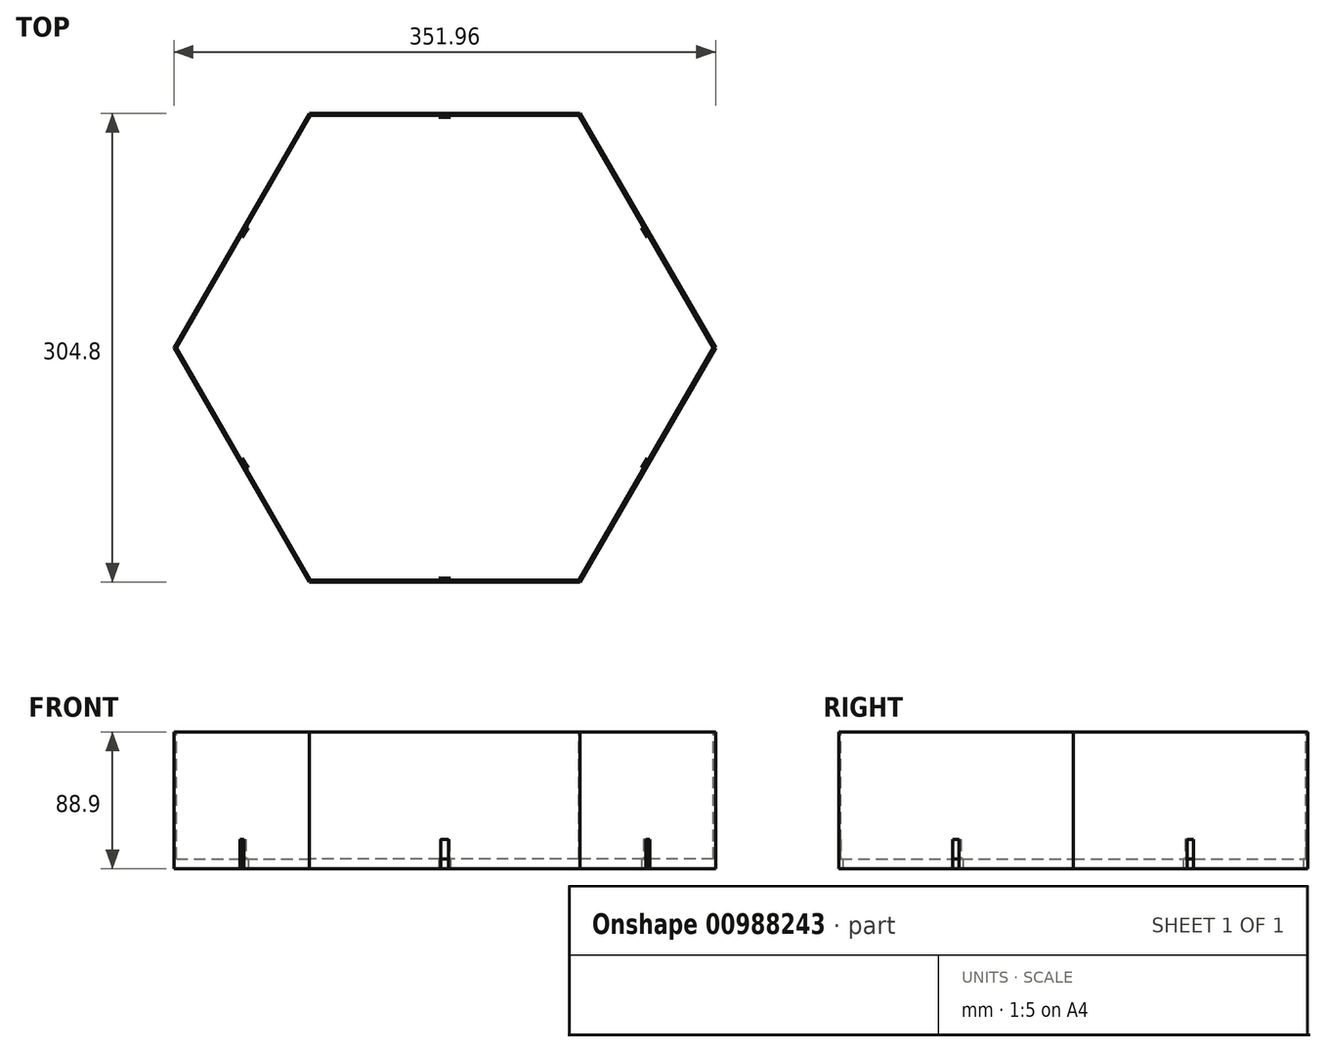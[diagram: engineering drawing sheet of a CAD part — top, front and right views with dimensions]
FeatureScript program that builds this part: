
annotation { "Feature Type Name" : "Feature", "Feature Type Description" : "" }
export const myFeature = defineFeature(function(context is Context, id is Id, definition is map)
    precondition{}
    {
        {
            var Q0;
            Q0=qCreatedBy(makeId("Top.planeOp"),FACE);
            var sketch = newSketch(context, id + "F0", { "sketchPlane" : qUnion([Q0])});
            skCircle(sketch, "E0.cCircle", {"center": v(0, 0) * mm, "radius": 152.4 * mm, "construction": true});
            skLineSegment(sketch, "E0.0", {"start": v(87.99, -152.4) * mm, "end": v(-87.99, -152.4) * mm});
            skLineSegment(sketch, "E0.1", {"start": v(-87.99, -152.4) * mm, "end": v(-175.98, 0) * mm});
            skLineSegment(sketch, "E0.2", {"start": v(-175.98, 0) * mm, "end": v(-87.99, 152.4) * mm});
            skLineSegment(sketch, "E0.3", {"start": v(-87.99, 152.4) * mm, "end": v(87.99, 152.4) * mm});
            skLineSegment(sketch, "E0.4", {"start": v(87.99, 152.4) * mm, "end": v(175.98, 0) * mm});
            skLineSegment(sketch, "E0.5", {"start": v(175.98, 0) * mm, "end": v(87.99, -152.4) * mm});
            skPoint(sketch, "E0.0.midPoint", {"position": v(0, -152.4) * mm});
            skSolve(sketch);
        }
        {
            var Q0;
            Q0=makeQuery(id+"F0.imprint","IMPRINT",FACE,{"disambiguationData":[TD([[makeQuery(id+"F0.imprint","IMPRINT",EDGE,{"derivedFrom":sQuery(id+"F0.wireOp",EDGE,"E0.0")}),-1.0]])]});
            extrude(context, id + "F1", {"entities" : qUnion([Q0]), "depth" : 88.9 * mm, "offsetDistance" : 25.4 * mm});
        }
        {
            var Q0;
            Q0=makeQuery(id+"F1.opExtrude","CAP_FACE",FACE,{"disambiguationData":[OSD([sQuery(id+"F0.wireOp",EDGE,"E0.0"),sQuery(id+"F0.wireOp",EDGE,"E0.1"),sQuery(id+"F0.wireOp",EDGE,"E0.2"),sQuery(id+"F0.wireOp",EDGE,"E0.3"),sQuery(id+"F0.wireOp",EDGE,"E0.4"),sQuery(id+"F0.wireOp",EDGE,"E0.5")])],"isStart":true});
            var sketch = newSketch(context, id + "F2", { "sketchPlane" : qUnion([Q0])});
            skLineSegment(sketch, "E1", {"start": v(0, 152.4) * mm, "end": v(0, -152.4) * mm});
            skLineSegment(sketch, "E2", {"start": v(-131.98, -76.2) * mm, "end": v(131.98, 76.2) * mm});
            skLineSegment(sketch, "E3", {"start": v(-131.98, 76.2) * mm, "end": v(131.98, -76.2) * mm});
            skLineSegment(sketch, "E4", {"start": v(87.99, 152.4) * mm, "end": v(-87.99, -152.4) * mm});
            skLineSegment(sketch, "E5", {"start": v(-87.99, 152.4) * mm, "end": v(87.99, -152.4) * mm});
            skLineSegment(sketch, "E6", {"start": v(-131.98, 76.2) * mm, "end": v(-129.78, 74.93) * mm});
            skLineSegment(sketch, "E7", {"start": v(-129.78, 74.93) * mm, "end": v(-127.88, 78.23) * mm});
            skLineSegment(sketch, "E8", {"start": v(-131.98, 76.2) * mm, "end": v(-130.71, 78.4) * mm});
            skLineSegment(sketch, "E9", {"start": v(-130.71, 78.4) * mm, "end": v(-127.88, 78.23) * mm});
            skLineSegment(sketch, "E10.MirrorCS", {"start": v(-129.78, 74.93) * mm, "end": v(-131.69, 71.63) * mm});
            skLineSegment(sketch, "E11.MirrorCS", {"start": v(-133.25, 74) * mm, "end": v(-131.69, 71.63) * mm});
            skLineSegment(sketch, "E12.MirrorCS", {"start": v(-131.98, 76.2) * mm, "end": v(-133.25, 74) * mm});
            skLineSegment(sketch, "E13.MirrorCS", {"start": v(129.78, -74.93) * mm, "end": v(131.69, -71.63) * mm});
            skLineSegment(sketch, "E14.MirrorCS", {"start": v(133.25, -74) * mm, "end": v(131.69, -71.63) * mm});
            skLineSegment(sketch, "E15.MirrorCS", {"start": v(131.98, -76.2) * mm, "end": v(133.25, -74) * mm});
            skLineSegment(sketch, "E16.MirrorCS", {"start": v(131.98, -76.2) * mm, "end": v(130.71, -78.4) * mm});
            skLineSegment(sketch, "E17.MirrorCS", {"start": v(130.71, -78.4) * mm, "end": v(127.88, -78.23) * mm});
            skLineSegment(sketch, "E18.MirrorCS", {"start": v(129.78, -74.93) * mm, "end": v(127.88, -78.23) * mm});
            skLineSegment(sketch, "E19", {"start": v(0, 152.4) * mm, "end": v(0, 149.86) * mm});
            skLineSegment(sketch, "E20", {"start": v(0, 149.86) * mm, "end": v(3.81, 149.86) * mm});
            skLineSegment(sketch, "E21", {"start": v(0, 152.4) * mm, "end": v(2.54, 152.4) * mm});
            skLineSegment(sketch, "E22", {"start": v(2.54, 152.4) * mm, "end": v(3.81, 149.86) * mm});
            skLineSegment(sketch, "E23.MirrorCS", {"start": v(0, 149.86) * mm, "end": v(-3.8, 149.86) * mm});
            skLineSegment(sketch, "E24.MirrorCS", {"start": v(-2.54, 152.4) * mm, "end": v(-3.8, 149.86) * mm});
            skLineSegment(sketch, "E25.MirrorCS", {"start": v(0, 152.4) * mm, "end": v(-2.54, 152.4) * mm});
            skLineSegment(sketch, "E26.MirrorCS", {"start": v(0, -149.86) * mm, "end": v(-3.8, -149.86) * mm});
            skLineSegment(sketch, "E27.MirrorCS", {"start": v(0, -149.86) * mm, "end": v(3.81, -149.86) * mm});
            skLineSegment(sketch, "E28.MirrorCS", {"start": v(-2.54, -152.4) * mm, "end": v(-3.8, -149.86) * mm});
            skLineSegment(sketch, "E29.MirrorCS", {"start": v(2.54, -152.4) * mm, "end": v(3.81, -149.86) * mm});
            skLineSegment(sketch, "E30.MirrorCS", {"start": v(0, -152.4) * mm, "end": v(-2.54, -152.4) * mm});
            skLineSegment(sketch, "E31.MirrorCS", {"start": v(0, -152.4) * mm, "end": v(2.54, -152.4) * mm});
            skLineSegment(sketch, "E32", {"start": v(-131.98, -76.2) * mm, "end": v(-129.78, -74.93) * mm});
            skLineSegment(sketch, "E33", {"start": v(-129.78, -74.93) * mm, "end": v(-131.69, -71.63) * mm});
            skLineSegment(sketch, "E34", {"start": v(-131.98, -76.2) * mm, "end": v(-133.25, -74) * mm});
            skLineSegment(sketch, "E35", {"start": v(-133.25, -74) * mm, "end": v(-131.69, -71.63) * mm});
            skLineSegment(sketch, "E36.MirrorCS", {"start": v(-129.78, -74.93) * mm, "end": v(-127.88, -78.23) * mm});
            skLineSegment(sketch, "E37.MirrorCS", {"start": v(-130.71, -78.4) * mm, "end": v(-127.88, -78.23) * mm});
            skLineSegment(sketch, "E38.MirrorCS", {"start": v(-131.98, -76.2) * mm, "end": v(-130.71, -78.4) * mm});
            skLineSegment(sketch, "E39.MirrorCS", {"start": v(129.78, 74.93) * mm, "end": v(131.69, 71.63) * mm});
            skLineSegment(sketch, "E40.MirrorCS", {"start": v(133.25, 74) * mm, "end": v(131.69, 71.63) * mm});
            skLineSegment(sketch, "E41.MirrorCS", {"start": v(131.98, 76.2) * mm, "end": v(133.25, 74) * mm});
            skLineSegment(sketch, "E42.MirrorCS", {"start": v(131.98, 76.2) * mm, "end": v(130.71, 78.4) * mm});
            skLineSegment(sketch, "E43.MirrorCS", {"start": v(130.71, 78.4) * mm, "end": v(127.88, 78.23) * mm});
            skLineSegment(sketch, "E44.MirrorCS", {"start": v(129.78, 74.93) * mm, "end": v(127.88, 78.23) * mm});
            skSolve(sketch);
        }
        {
            var Q0;
            {var subQ0=sQuery(id+"F2.wireOp",EDGE,"E33");Q0=makeQuery(id+"F2.imprint","IMPRINT",FACE,{"disambiguationData":[TD([[makeQuery(id+"F2.imprint","IMPRINT",EDGE,{"derivedFrom":subQ0}),1.0]])]});}
            var Q1;
            {var subQ0=sQuery(id+"F2.wireOp",EDGE,"E36.MirrorCS");Q1=makeQuery(id+"F2.imprint","IMPRINT",FACE,{"disambiguationData":[TD([[makeQuery(id+"F2.imprint","IMPRINT",EDGE,{"derivedFrom":subQ0}),-1.0]])]});}
            var Q2;
            {var subQ0=sQuery(id+"F2.wireOp",EDGE,"E10.MirrorCS");Q2=makeQuery(id+"F2.imprint","IMPRINT",FACE,{"disambiguationData":[TD([[makeQuery(id+"F2.imprint","IMPRINT",EDGE,{"derivedFrom":subQ0}),-1.0]])]});}
            var Q3;
            {var subQ0=sQuery(id+"F2.wireOp",EDGE,"E7");Q3=makeQuery(id+"F2.imprint","IMPRINT",FACE,{"disambiguationData":[TD([[makeQuery(id+"F2.imprint","IMPRINT",EDGE,{"derivedFrom":subQ0}),1.0]])]});}
            var Q4;
            {var subQ0=sQuery(id+"F2.wireOp",EDGE,"E23.MirrorCS");Q4=makeQuery(id+"F2.imprint","IMPRINT",FACE,{"disambiguationData":[TD([[makeQuery(id+"F2.imprint","IMPRINT",EDGE,{"derivedFrom":subQ0}),-1.0]])]});}
            var Q5;
            {var subQ0=sQuery(id+"F2.wireOp",EDGE,"E20");Q5=makeQuery(id+"F2.imprint","IMPRINT",FACE,{"disambiguationData":[TD([[makeQuery(id+"F2.imprint","IMPRINT",EDGE,{"derivedFrom":subQ0}),1.0]])]});}
            var Q6;
            {var subQ2=sQuery(id+"F2.wireOp",EDGE,"E42.MirrorCS");Q6=makeQuery(id+"F2.imprint","IMPRINT",FACE,{"disambiguationData":[TD([[makeQuery(id+"F2.imprint","IMPRINT",EDGE,{"derivedFrom":subQ2}),1.0]])]});}
            var Q7;
            {var subQ0=sQuery(id+"F2.wireOp",EDGE,"E39.MirrorCS");Q7=makeQuery(id+"F2.imprint","IMPRINT",FACE,{"disambiguationData":[TD([[makeQuery(id+"F2.imprint","IMPRINT",EDGE,{"derivedFrom":subQ0}),1.0]])]});}
            var Q8;
            {var subQ0=sQuery(id+"F2.wireOp",EDGE,"E13.MirrorCS");Q8=makeQuery(id+"F2.imprint","IMPRINT",FACE,{"disambiguationData":[TD([[makeQuery(id+"F2.imprint","IMPRINT",EDGE,{"derivedFrom":subQ0}),-1.0]])]});}
            var Q9;
            {var subQ2=sQuery(id+"F2.wireOp",EDGE,"E16.MirrorCS");Q9=makeQuery(id+"F2.imprint","IMPRINT",FACE,{"disambiguationData":[TD([[makeQuery(id+"F2.imprint","IMPRINT",EDGE,{"derivedFrom":subQ2}),1.0]])]});}
            var Q10;
            {var subQ0=sQuery(id+"F2.wireOp",EDGE,"E27.MirrorCS");Q10=makeQuery(id+"F2.imprint","IMPRINT",FACE,{"disambiguationData":[TD([[makeQuery(id+"F2.imprint","IMPRINT",EDGE,{"derivedFrom":subQ0}),-1.0]])]});}
            var Q11;
            {var subQ0=sQuery(id+"F2.wireOp",EDGE,"E26.MirrorCS");Q11=makeQuery(id+"F2.imprint","IMPRINT",FACE,{"disambiguationData":[TD([[makeQuery(id+"F2.imprint","IMPRINT",EDGE,{"derivedFrom":subQ0}),1.0]])]});}
            extrude(context, id + "F3", {"entities" : qUnion([Q0, Q1, Q2, Q3, Q4, Q5, Q6, Q7, Q8, Q9, Q10, Q11]), "operationType" : NewBodyOperationType.REMOVE, "oppositeDirection" : true, "depth" : 19.05 * mm, "offsetDistance" : 25.4 * mm});
        }
        {
            var Q0;
            Q0=makeQuery(id+"F1.opExtrude","CAP_FACE",FACE,{"disambiguationData":[OSD([sQuery(id+"F0.wireOp",EDGE,"E0.0"),sQuery(id+"F0.wireOp",EDGE,"E0.1"),sQuery(id+"F0.wireOp",EDGE,"E0.2"),sQuery(id+"F0.wireOp",EDGE,"E0.3"),sQuery(id+"F0.wireOp",EDGE,"E0.4"),sQuery(id+"F0.wireOp",EDGE,"E0.5")])],"isStart":false});
            var sketch = newSketch(context, id + "F4", { "sketchPlane" : qUnion([Q0])});
            skCircle(sketch, "E45.cCircle", {"center": v(0, 0) * mm, "radius": 151.13 * mm, "construction": true});
            skLineSegment(sketch, "E45.0", {"start": v(87.25, -151.13) * mm, "end": v(-87.25, -151.13) * mm});
            skLineSegment(sketch, "E45.1", {"start": v(-87.25, -151.13) * mm, "end": v(-174.5, 0) * mm});
            skLineSegment(sketch, "E45.2", {"start": v(-174.5, 0) * mm, "end": v(-87.25, 151.13) * mm});
            skLineSegment(sketch, "E45.3", {"start": v(-87.25, 151.13) * mm, "end": v(87.25, 151.13) * mm});
            skLineSegment(sketch, "E45.4", {"start": v(87.25, 151.13) * mm, "end": v(174.5, 0) * mm});
            skLineSegment(sketch, "E45.5", {"start": v(174.5, 0) * mm, "end": v(87.25, -151.13) * mm});
            skPoint(sketch, "E45.0.midPoint", {"position": v(0, -151.13) * mm});
            skSolve(sketch);
        }
        {
            var Q0;
            Q0=makeQuery(id+"F4.imprint","IMPRINT",FACE,{"disambiguationData":[TD([[makeQuery(id+"F4.imprint","IMPRINT",EDGE,{"derivedFrom":sQuery(id+"F4.wireOp",EDGE,"E45.0")}),-1.0]])]});
            extrude(context, id + "F5", {"entities" : qUnion([Q0]), "operationType" : NewBodyOperationType.REMOVE, "oppositeDirection" : true, "depth" : 82.55 * mm, "offsetDistance" : 25.4 * mm});
        }
    });
